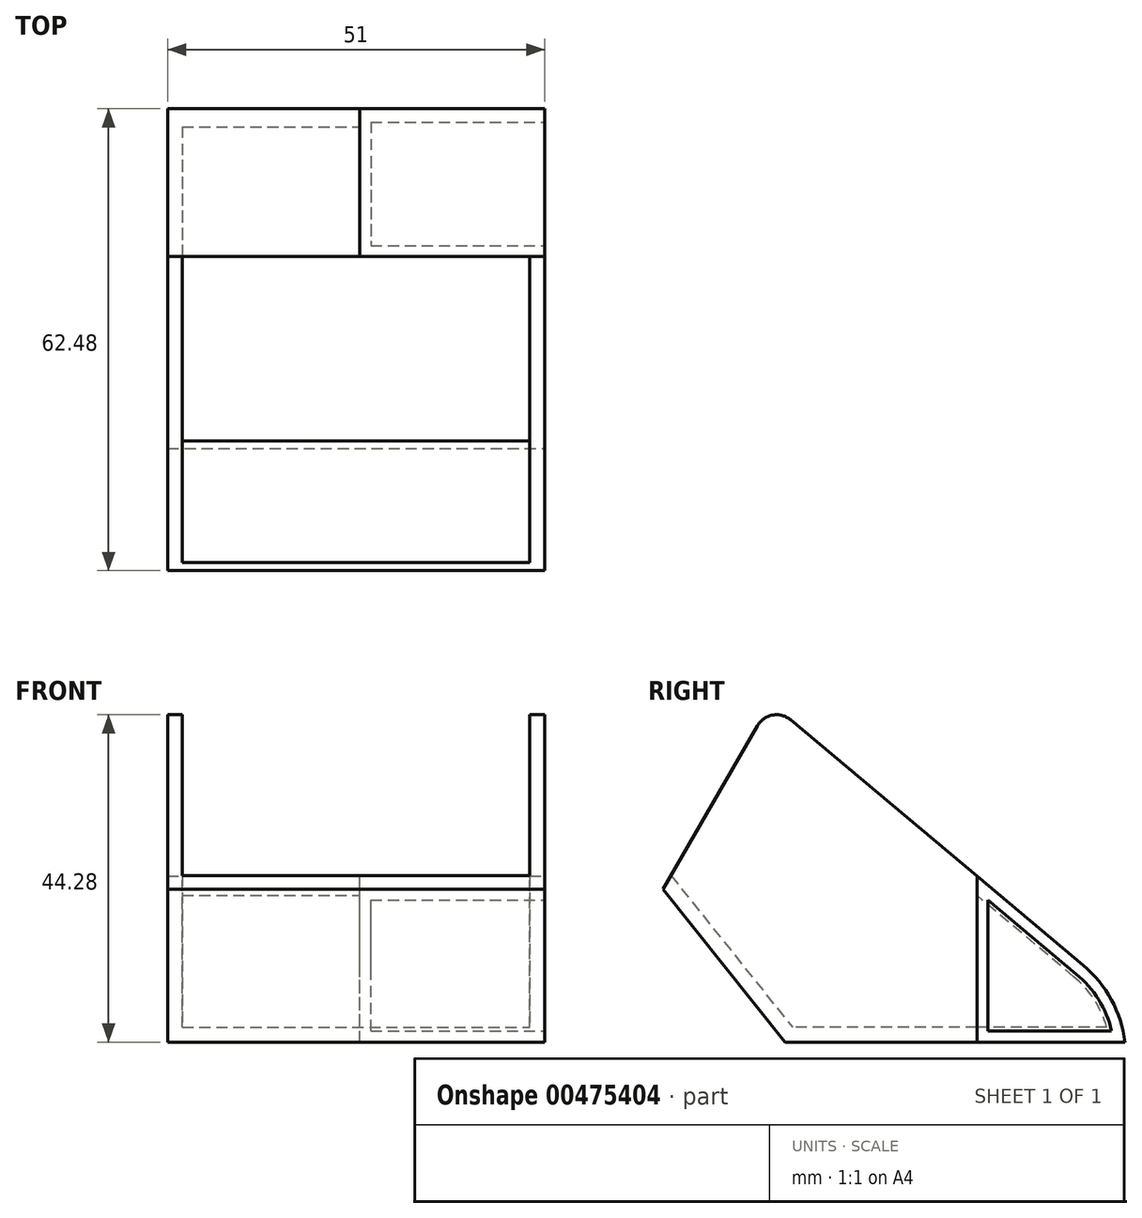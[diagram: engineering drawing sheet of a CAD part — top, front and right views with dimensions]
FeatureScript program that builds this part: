
annotation { "Feature Type Name" : "Feature", "Feature Type Description" : "" }
export const myFeature = defineFeature(function(context is Context, id is Id, definition is map)
    precondition{}
    {
        {
            var Q0;
            Q0=qCreatedBy(makeId("Right.planeOp"),FACE);
            var sketch = newSketch(context, id + "F0", { "sketchPlane" : qUnion([Q0])});
            skLineSegment(sketch, "E0.0", {"start": v(-16.55, 20.68) * mm, "end": v(-3.79, 42.78) * mm});
            skLineSegment(sketch, "E1.0", {"start": v(-16.55, 20.68) * mm, "end": v(0, 0) * mm});
            skLineSegment(sketch, "E2.0", {"start": v(45.93, 0) * mm, "end": v(0, 0) * mm});
            skArc(sketch, "E3.0", {"start": v(45.93, 0) * mm, "mid": v(44.11, 5.72) * mm, "end": v(40.32, 10.36) * mm});
            skLineSegment(sketch, "E4.0", {"start": v(40.32, 10.36) * mm, "end": v(0.74, 43.58) * mm});
            skArc(sketch, "E5.0", {"start": v(0.74, 43.58) * mm, "mid": v(-1.71, 44.24) * mm, "end": v(-3.79, 42.78) * mm});
            skPoint(sketch, "E6.endSnap0", {"position": v(22.96, 0) * mm});
            skPoint(sketch, "E7", {"position": v(11.77, 0.94) * mm});
            skLineSegment(sketch, "E8", {"start": v(25.93, 0) * mm, "end": v(25.93, 22.44) * mm});
            skSolve(sketch);
        }
        {
            var Q0;
            Q0=makeQuery(id+"F0.imprint","IMPRINT",FACE,{"disambiguationData":[TD([[makeQuery(id+"F0.imprint","IMPRINT",EDGE,{"derivedFrom":sQuery(id+"F0.wireOp",EDGE,"E0.0")}),-1.0]])]});
            extrude(context, id + "F1", {"entities" : qUnion([Q0]), "oppositeDirection" : true, "depth" : 51 * mm});
        }
        {
            var Q0;
            {var subQ0=sQuery(id+"F0.wireOp",EDGE,"E3.0");Q0=makeQuery(id+"F0.imprint","IMPRINT",FACE,{"disambiguationData":[TD([[makeQuery(id+"F0.imprint","IMPRINT",EDGE,{"derivedFrom":subQ0}),1.0]])]});}
            extrude(context, id + "F2", {"entities" : qUnion([Q0]), "oppositeDirection" : true, "depth" : 51 * mm});
        }
        {
            var Q0;
            Q0=makeQuery(id+"F1.opExtrude","SWEPT_FACE",FACE,{"disambiguationData":[OSD([sQuery(id+"F0.wireOp",EDGE,"E4.0")])]});
            var Q1;
            Q1=makeQuery(id+"F1.opExtrude","SWEPT_FACE",FACE,{"disambiguationData":[OSD([sQuery(id+"F0.wireOp",EDGE,"E0.0")])]});
            var Q2;
            Q2=makeQuery(id+"F1.opExtrude","SWEPT_FACE",FACE,{"disambiguationData":[OSD([sQuery(id+"F0.wireOp",EDGE,"E5.0")])]});
            var Q3;
            Q3=makeQuery(id+"F1.opExtrude","SWEPT_FACE",FACE,{"disambiguationData":[OSD([sQuery(id+"F0.wireOp",EDGE,"E8")])]});
            shell(context, id + "F3", {"entities" : qUnion([Q0, Q1, Q2, Q3]), "thickness" : 2 * mm});
        }
        {
            var Q0;
            {var subQ0=sQuery(id+"F0.wireOp",EDGE,"E3.0");Q0=makeQuery(id+"F0.imprint","IMPRINT",FACE,{"disambiguationData":[TD([[makeQuery(id+"F0.imprint","IMPRINT",EDGE,{"derivedFrom":subQ0}),1.0]])]});}
            extrude(context, id + "F4", {"entities" : qUnion([Q0]), "operationType" : NewBodyOperationType.REMOVE, "oppositeDirection" : true, "depth" : 25 * mm});
        }
        {
            var Q0;
            {var subQ0=sQuery(id+"F0.wireOp",EDGE,"E3.0");Q0=makeQuery(id+"F0.imprint","IMPRINT",FACE,{"disambiguationData":[TD([[makeQuery(id+"F0.imprint","IMPRINT",EDGE,{"derivedFrom":subQ0}),1.0]])]});}
            extrude(context, id + "F5", {"entities" : qUnion([Q0]), "oppositeDirection" : true, "depth" : 25 * mm});
        }
        {
            var Q0;
            Q0=makeQuery(id+"F2.opExtrude","SWEPT_FACE",FACE,{"disambiguationData":[OSD([sQuery(id+"F0.wireOp",EDGE,"E8")])]});
            var Q1;
            Q1=makeQuery(id+"F4.boolean.opBoolean","COPY",FACE,{"derivedFrom":makeQuery(id+"F4.opExtrude","CAP_FACE",FACE,{"disambiguationData":[OSD([sQuery(id+"F0.wireOp",EDGE,"E2.0"),sQuery(id+"F0.wireOp",EDGE,"E3.0"),sQuery(id+"F0.wireOp",EDGE,"E4.0"),sQuery(id+"F0.wireOp",EDGE,"E8")])],"isStart":false})});
            shell(context, id + "F6", {"entities" : qUnion([Q0, Q1]), "thickness" : 2 * mm});
        }
        {
            var Q0;
            Q0=makeQuery(id+"F5.opExtrude","CAP_FACE",FACE,{"disambiguationData":[OSD([sQuery(id+"F0.wireOp",EDGE,"E2.0"),sQuery(id+"F0.wireOp",EDGE,"E3.0"),sQuery(id+"F0.wireOp",EDGE,"E4.0"),sQuery(id+"F0.wireOp",EDGE,"E8")])],"isStart":true});
            shell(context, id + "F7", {"entities" : qUnion([Q0]), "thickness" : 1.5 * mm});
        }
    });
